# Revit family: NLRS_27_GM_LIB_GSI_MR
name_source: partatom
category: Generic Models
revit_build: Autodesk Revit 2017 (Build: 20190507_1515(x64)
units: mm (PartAtom-declared; Revit-internal decimal feet)

## family parameters
Can host rebar = No
Cut with Voids When Loaded = Yes
Part Type = Normal
Room Calculation Point = No
Round Connector Dimension = Use Diameter
Shared = No

## types (2) — shared parameters
Assembly Code = 27.16
Description = GSI Goot
Hoek_VK_Goot = 20.00°
IfcExportAs = IfcFlowsegment
Manufacturer = Meilof Riks bv
Model = GSI
NLRS_C_Binnenbak = RAL 9010
NLRS_C_Materiaal = RAL 9010
Type Image = <None>
URL = https://www.meilofriks.nl
Vorm_Goot_R = 01 : 3_→_Hoek_R

## per-type parameters (varying)
| type | Breedte_goot | Diepte_bak | Hoogte_AK | Hoogte_VK | Set_Diepte_bak | Vorm_Goot_L | Vorm_Goot_L-R | set_Hoogte_AK |
| GI280 | 280 mm  [stored 0.918635 ft] | 88 mm  [stored 0.288714 ft] | 215 mm | 186 mm  [stored 0.610236 ft] | 88 mm  [stored 0.288714 ft] | 01 : 2_←_Hoek_L | 01 : 4_↔_Hoek_L-R | 215 mm |
| GI325 | 325 mm | 74 mm  [stored 0.242782 ft] | 221 mm | 197 mm | 74 mm  [stored 0.242782 ft] | 01 : 3_→_Hoek_R | 01 : 3_→_Hoek_R | 222 mm |

note: [stored X ft] marks values corroborated as IEEE doubles in the binary element streams (Revit-internal decimal feet)

## geometry (parser evidence)
native form markers: Sweep x20
no freeform markers — native parametric forms only
